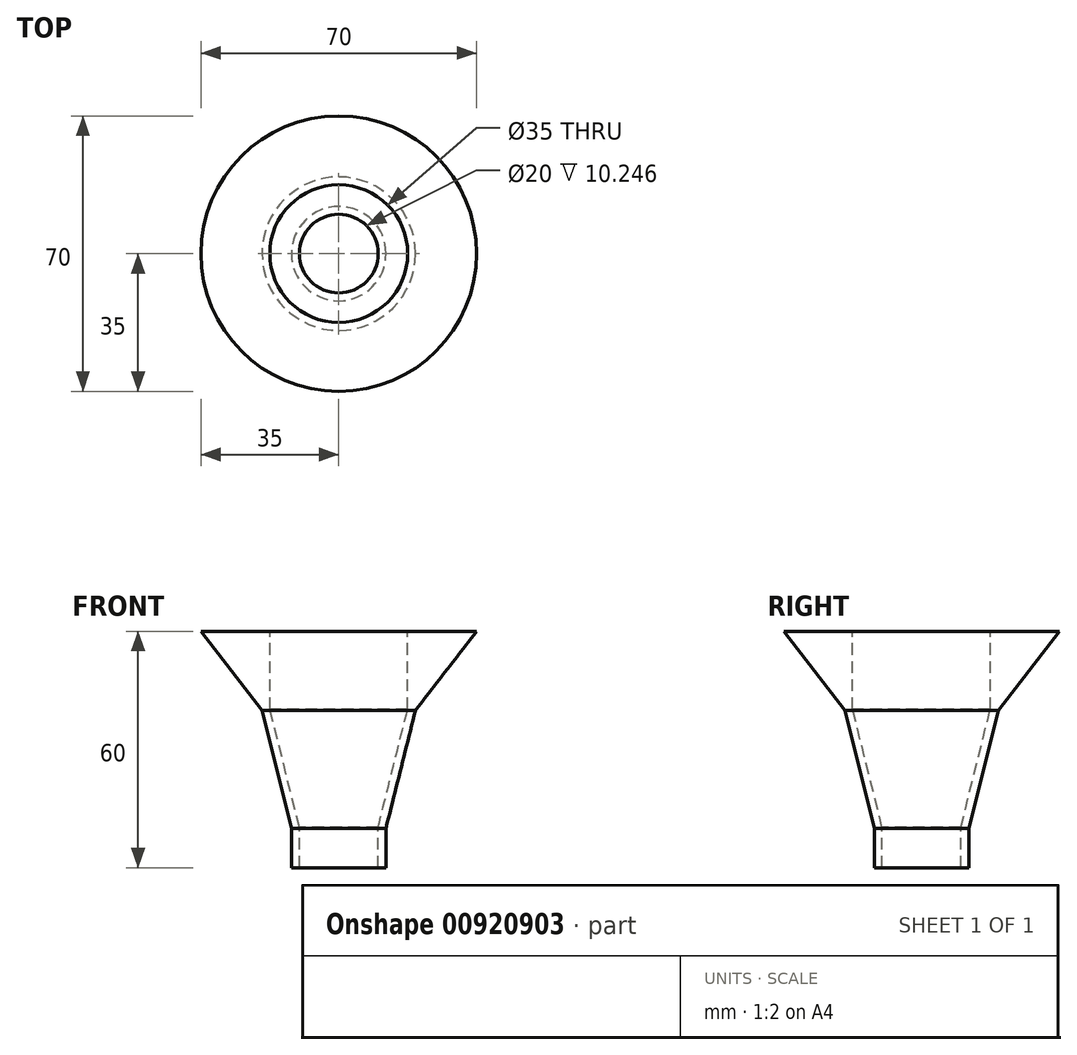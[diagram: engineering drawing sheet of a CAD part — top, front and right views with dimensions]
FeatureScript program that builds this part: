
annotation { "Feature Type Name" : "Feature", "Feature Type Description" : "" }
export const myFeature = defineFeature(function(context is Context, id is Id, definition is map)
    precondition{}
    {
        {
            var Q0;
            Q0=qCreatedBy(makeId("Front.planeOp"),FACE);
            var sketch = newSketch(context, id + "F0", { "sketchPlane" : qUnion([Q0])});
            skLineSegment(sketch, "E0", {"start": v(0, 57.79) * mm, "end": v(0, -44.66) * mm});
            skSolve(sketch);
        }
        {
            var Q0;
            Q0=qCreatedBy(makeId("Front.planeOp"),FACE);
            var sketch = newSketch(context, id + "F1", { "sketchPlane" : qUnion([Q0])});
            skLineSegment(sketch, "E1", {"start": v(10, 10.25) * mm, "end": v(10, 0) * mm});
            skLineSegment(sketch, "E2", {"start": v(10, 0) * mm, "end": v(12, 0) * mm});
            skLineSegment(sketch, "E3", {"start": v(12, 0) * mm, "end": v(12, 10) * mm});
            skLineSegment(sketch, "E4", {"start": v(12, 10) * mm, "end": v(19.5, 40) * mm});
            skLineSegment(sketch, "E5", {"start": v(19.5, 40) * mm, "end": v(19.5, 60) * mm, "construction": true});
            skLineSegment(sketch, "E6", {"start": v(19.5, 60) * mm, "end": v(17.5, 60) * mm});
            skLineSegment(sketch, "E7", {"start": v(17.5, 60) * mm, "end": v(17.5, 40.25) * mm});
            skLineSegment(sketch, "E8", {"start": v(17.5, 40.25) * mm, "end": v(10, 10.25) * mm});
            skLineSegment(sketch, "E9", {"start": v(19.5, 60) * mm, "end": v(35, 60) * mm});
            skLineSegment(sketch, "E10", {"start": v(35, 60) * mm, "end": v(19.5, 40) * mm});
            skSolve(sketch);
        }
        {
            var Q0;
            Q0=makeQuery(id+"F1.imprint","IMPRINT",FACE,{"disambiguationData":[TD([[makeQuery(id+"F1.imprint","IMPRINT",EDGE,{"derivedFrom":sQuery(id+"F1.wireOp",EDGE,"E1")}),1.0]])]});
            var Q1;
            Q1=sQuery(id+"F0.wireOp",EDGE,"E0");
            revolve(context, id + "F2", {"surfaceOperationType" : NewSurfaceOperationType.NEW, "entities" : qUnion([Q0]), "axis" : qUnion([Q1]), "revolveType" : RevolveType.FULL});
        }
    });
